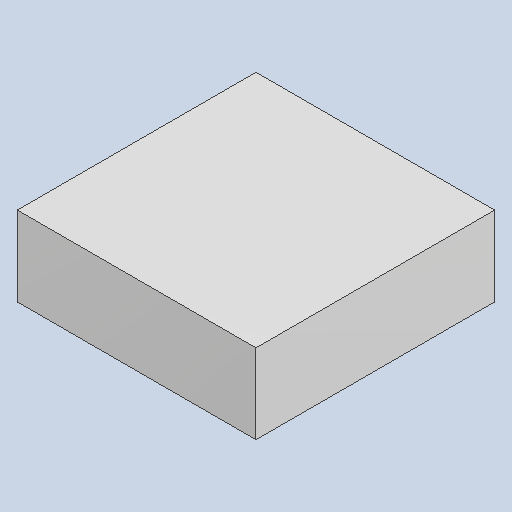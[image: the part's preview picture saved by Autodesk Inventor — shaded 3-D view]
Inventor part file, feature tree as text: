
AUTODESK INVENTOR PART (.ipt)
format: ipt  version: 2023.4 (Build 274418000, 418)  size: 79,872 bytes
history: native  units: mm
features: extrude x1
ambient origin geometry x8: Origin, YZ Plane, XZ Plane, XY Plane, X Axis, Y Axis, Z Axis, Center Point
bodies: Solid1 (feature_tree)
feature tree (1):
  extrude  "Extruded_40"  [1 undecoded]
note: 1 required parameter value undecoded (feature->parameter linkage not recoverable at this tier; creation-order binding heuristic only, values carry confidence <= 0.55)
